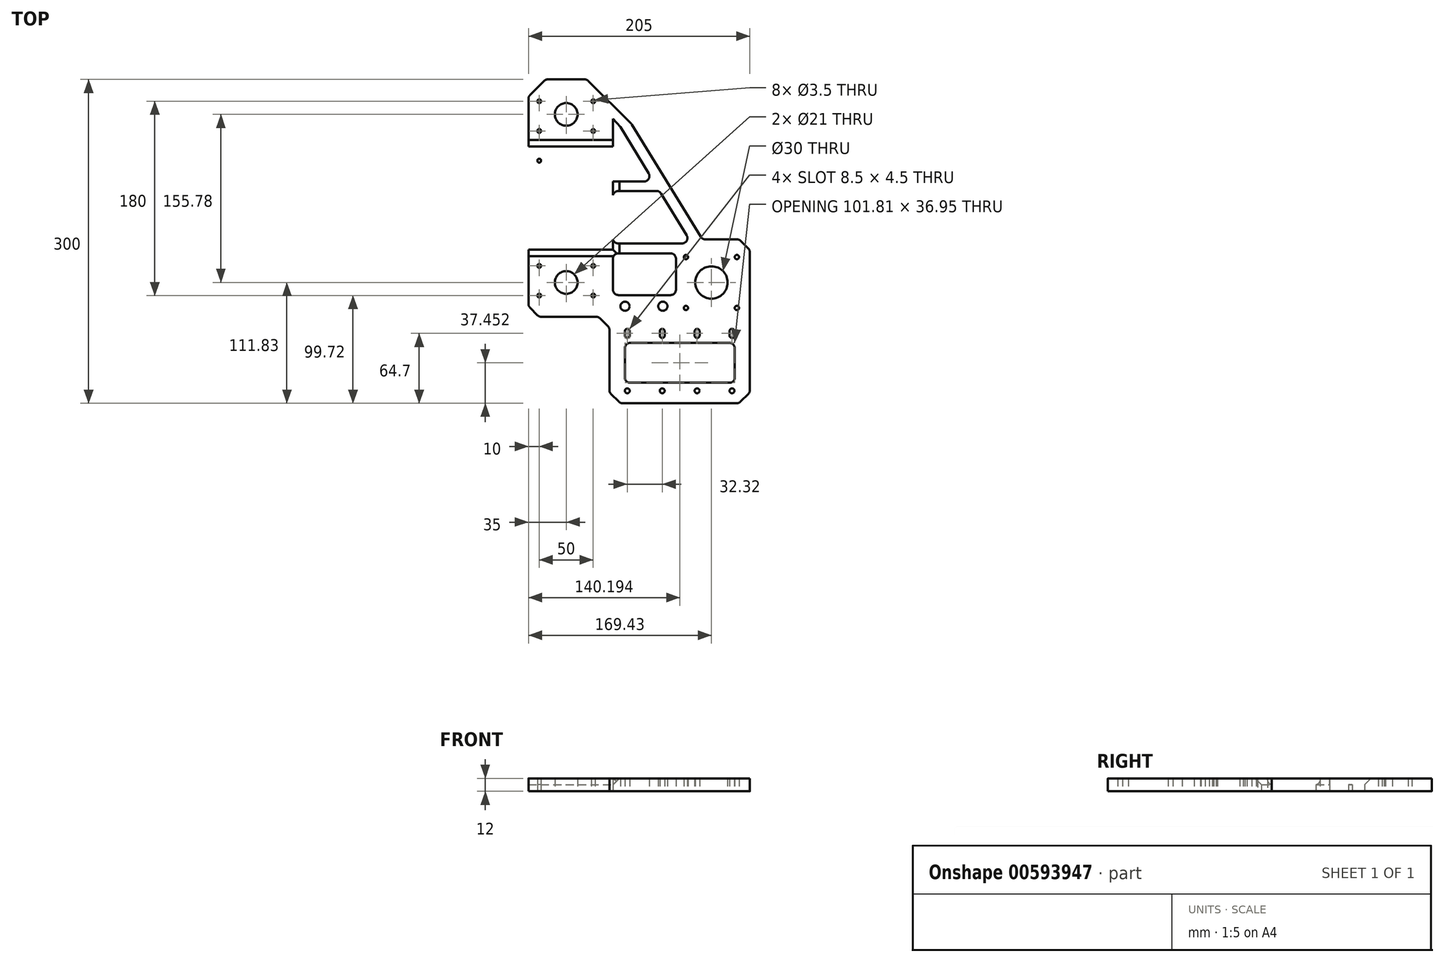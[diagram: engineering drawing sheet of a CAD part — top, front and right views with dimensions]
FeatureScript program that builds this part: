
annotation { "Feature Type Name" : "Feature", "Feature Type Description" : "" }
export const myFeature = defineFeature(function(context is Context, id is Id, definition is map)
    precondition{}
    {
        {
            var Q0;
            Q0=qCreatedBy(makeId("Top.planeOp"),FACE);
            var sketch = newSketch(context, id + "F0", { "sketchPlane" : qUnion([Q0])});
            skLineSegment(sketch, "E0", {"start": v(93.96, -148.54) * mm, "end": v(101.04, -141.46) * mm});
            skLineSegment(sketch, "E1", {"start": v(90.43, -150) * mm, "end": v(-15.43, -150) * mm});
            skLineSegment(sketch, "E2", {"start": v(-26.04, -141.46) * mm, "end": v(-18.96, -148.54) * mm});
            skLineSegment(sketch, "E3", {"start": v(-27.5, -137.93) * mm, "end": v(-27.5, -82.07) * mm});
            skLineSegment(sketch, "E4", {"start": v(-36.04, -71.46) * mm, "end": v(-28.96, -78.54) * mm});
            skLineSegment(sketch, "E5", {"start": v(-39.57, -70) * mm, "end": v(-90.43, -70) * mm});
            skLineSegment(sketch, "E6", {"start": v(-101.04, -61.46) * mm, "end": v(-93.96, -68.54) * mm});
            skLineSegment(sketch, "E7", {"start": v(-102.5, -57.93) * mm, "end": v(-102.5, 131.93) * mm});
            skLineSegment(sketch, "E8", {"start": v(-87.96, 148.54) * mm, "end": v(-101.04, 135.46) * mm});
            skLineSegment(sketch, "E9", {"start": v(-84.43, 150) * mm, "end": v(-50.57, 150) * mm});
            skLineSegment(sketch, "E10", {"start": v(-7.5, 109) * mm, "end": v(-47.04, 148.54) * mm});
            skLineSegment(sketch, "E11", {"start": v(-6.78, 108.09) * mm, "end": v(56.96, 4.21) * mm});
            skLineSegment(sketch, "E12", {"start": v(90.43, 1.83) * mm, "end": v(61.22, 1.83) * mm});
            skLineSegment(sketch, "E13", {"start": v(101.04, -6.7) * mm, "end": v(93.96, 0.37) * mm});
            skLineSegment(sketch, "E14", {"start": v(102.5, -10.24) * mm, "end": v(102.5, -137.93) * mm});
            skLineSegment(sketch, "E15", {"start": v(-13.2, -83.3) * mm, "end": v(-13.2, -87.3) * mm});
            skLineSegment(sketch, "E16", {"start": v(-8.7, -87.3) * mm, "end": v(-8.7, -83.3) * mm});
            skLineSegment(sketch, "E17", {"start": v(19.11, -83.3) * mm, "end": v(19.11, -87.3) * mm});
            skLineSegment(sketch, "E18", {"start": v(23.61, -87.3) * mm, "end": v(23.61, -83.3) * mm});
            skLineSegment(sketch, "E19", {"start": v(51.43, -83.3) * mm, "end": v(51.43, -87.3) * mm});
            skLineSegment(sketch, "E20", {"start": v(55.93, -87.3) * mm, "end": v(55.93, -83.3) * mm});
            skLineSegment(sketch, "E21", {"start": v(83.75, -83.3) * mm, "end": v(83.75, -87.3) * mm});
            skLineSegment(sketch, "E22", {"start": v(88.25, -87.3) * mm, "end": v(88.25, -83.3) * mm});
            skCircle(sketch, "E23", {"center": v(-42.5, 129.72) * mm, "radius": 1.75 * mm});
            skCircle(sketch, "E24", {"center": v(-92.5, 129.72) * mm, "radius": 1.75 * mm});
            skCircle(sketch, "E25", {"center": v(-92.5, 74.72) * mm, "radius": 1.75 * mm});
            skCircle(sketch, "E26", {"center": v(-92.5, 4.72) * mm, "radius": 1.75 * mm});
            skCircle(sketch, "E27", {"center": v(-92.5, -50.28) * mm, "radius": 1.75 * mm});
            skCircle(sketch, "E28", {"center": v(-42.5, -50.28) * mm, "radius": 1.75 * mm});
            skCircle(sketch, "E29", {"center": v(-42.5, 4.72) * mm, "radius": 1.75 * mm});
            skCircle(sketch, "E30", {"center": v(-42.5, 74.72) * mm, "radius": 1.75 * mm});
            skCircle(sketch, "E31", {"center": v(-92.5, 102.22) * mm, "radius": 1.75 * mm});
            skCircle(sketch, "E32", {"center": v(-42.5, 102.22) * mm, "radius": 1.75 * mm});
            skCircle(sketch, "E33", {"center": v(-67.5, 74.72) * mm, "radius": 1.75 * mm});
            skCircle(sketch, "E34", {"center": v(-92.5, 39.72) * mm, "radius": 1.75 * mm});
            skCircle(sketch, "E35", {"center": v(-42.5, 39.72) * mm, "radius": 1.75 * mm});
            skCircle(sketch, "E36", {"center": v(-92.5, -22.78) * mm, "radius": 1.75 * mm});
            skCircle(sketch, "E37", {"center": v(-42.5, -22.78) * mm, "radius": 1.75 * mm});
            skCircle(sketch, "E38", {"center": v(-67.5, 4.72) * mm, "radius": 1.75 * mm});
            skCircle(sketch, "E39", {"center": v(-10.96, -138.5) * mm, "radius": 2.25 * mm});
            skCircle(sketch, "E40", {"center": v(21.36, -138.5) * mm, "radius": 2.25 * mm});
            skCircle(sketch, "E41", {"center": v(53.68, -138.5) * mm, "radius": 2.25 * mm});
            skCircle(sketch, "E42", {"center": v(86, -138.5) * mm, "radius": 2.25 * mm});
            skCircle(sketch, "E43", {"center": v(-67.5, 39.72) * mm, "radius": 15 * mm});
            skCircle(sketch, "E44", {"center": v(-91.07, 63.3) * mm, "radius": 2 * mm});
            skCircle(sketch, "E45", {"center": v(-43.93, 63.3) * mm, "radius": 2 * mm});
            skCircle(sketch, "E46", {"center": v(-43.93, 16.15) * mm, "radius": 2 * mm});
            skCircle(sketch, "E47", {"center": v(-91.07, 16.15) * mm, "radius": 2 * mm});
            skCircle(sketch, "E48", {"center": v(-67.5, -38.17) * mm, "radius": 10.5 * mm});
            skCircle(sketch, "E49", {"center": v(-67.5, 117.61) * mm, "radius": 10.5 * mm});
            skCircle(sketch, "E50", {"center": v(-13.07, -60.17) * mm, "radius": 4.25 * mm});
            skCircle(sketch, "E51", {"center": v(21.93, -60.17) * mm, "radius": 4.25 * mm});
            skCircle(sketch, "E52", {"center": v(43.36, -14.6) * mm, "radius": 2 * mm});
            skCircle(sketch, "E53", {"center": v(90.5, -14.6) * mm, "radius": 2 * mm});
            skCircle(sketch, "E54", {"center": v(90.5, -61.74) * mm, "radius": 2 * mm});
            skCircle(sketch, "E55", {"center": v(43.36, -61.74) * mm, "radius": 2 * mm});
            skCircle(sketch, "E56", {"center": v(66.93, -38.17) * mm, "radius": 15 * mm});
            skArc(sketch, "E57", {"start": v(-8.7, -83.3) * mm, "mid": v(-10.96, -81.05) * mm, "end": v(-13.2, -83.3) * mm});
            skArc(sketch, "E58", {"start": v(-13.2, -87.3) * mm, "mid": v(-10.96, -89.55) * mm, "end": v(-8.7, -87.3) * mm});
            skArc(sketch, "E59", {"start": v(23.61, -83.3) * mm, "mid": v(21.36, -81.05) * mm, "end": v(19.11, -83.3) * mm});
            skArc(sketch, "E60", {"start": v(19.11, -87.3) * mm, "mid": v(21.36, -89.55) * mm, "end": v(23.61, -87.3) * mm});
            skArc(sketch, "E61", {"start": v(55.93, -83.3) * mm, "mid": v(53.68, -81.05) * mm, "end": v(51.43, -83.3) * mm});
            skArc(sketch, "E62", {"start": v(51.43, -87.3) * mm, "mid": v(53.68, -89.55) * mm, "end": v(55.93, -87.3) * mm});
            skArc(sketch, "E63", {"start": v(88.25, -83.3) * mm, "mid": v(86, -81.05) * mm, "end": v(83.75, -83.3) * mm});
            skArc(sketch, "E64", {"start": v(83.75, -87.3) * mm, "mid": v(86, -89.55) * mm, "end": v(88.25, -87.3) * mm});
            skPoint(sketch, "E65.visualSharp", {"position": v(-48.5, 150) * mm});
            skArc(sketch, "E65.filletArc", {"start": v(-47.04, 148.54) * mm, "mid": v(-48.66, 149.62) * mm, "end": v(-50.57, 150) * mm});
            skPoint(sketch, "E66.visualSharp", {"position": v(-86.5, 150) * mm});
            skArc(sketch, "E66.filletArc", {"start": v(-84.43, 150) * mm, "mid": v(-86.34, 149.62) * mm, "end": v(-87.96, 148.54) * mm});
            skPoint(sketch, "E67.visualSharp", {"position": v(-102.5, 134) * mm});
            skArc(sketch, "E67.filletArc", {"start": v(-101.04, 135.46) * mm, "mid": v(-102.12, 133.84) * mm, "end": v(-102.5, 131.93) * mm});
            skPoint(sketch, "E68.visualSharp", {"position": v(-102.5, -60) * mm});
            skArc(sketch, "E68.filletArc", {"start": v(-102.5, -57.93) * mm, "mid": v(-102.12, -59.84) * mm, "end": v(-101.04, -61.46) * mm});
            skPoint(sketch, "E69.visualSharp", {"position": v(-92.5, -70) * mm});
            skArc(sketch, "E69.filletArc", {"start": v(-93.96, -68.54) * mm, "mid": v(-92.34, -69.62) * mm, "end": v(-90.43, -70) * mm});
            skPoint(sketch, "E70.visualSharp", {"position": v(-37.5, -70) * mm});
            skArc(sketch, "E70.filletArc", {"start": v(-36.04, -71.46) * mm, "mid": v(-37.66, -70.38) * mm, "end": v(-39.57, -70) * mm});
            skPoint(sketch, "E71.visualSharp", {"position": v(-27.5, -80) * mm});
            skArc(sketch, "E71.filletArc", {"start": v(-27.5, -82.07) * mm, "mid": v(-27.88, -80.16) * mm, "end": v(-28.96, -78.54) * mm});
            skPoint(sketch, "E72.visualSharp", {"position": v(-27.5, -140) * mm});
            skArc(sketch, "E72.filletArc", {"start": v(-27.5, -137.93) * mm, "mid": v(-27.12, -139.84) * mm, "end": v(-26.04, -141.46) * mm});
            skPoint(sketch, "E73.visualSharp", {"position": v(-17.5, -150) * mm});
            skArc(sketch, "E73.filletArc", {"start": v(-18.96, -148.54) * mm, "mid": v(-17.34, -149.62) * mm, "end": v(-15.43, -150) * mm});
            skPoint(sketch, "E74.visualSharp", {"position": v(92.5, -150) * mm});
            skArc(sketch, "E74.filletArc", {"start": v(90.43, -150) * mm, "mid": v(92.34, -149.62) * mm, "end": v(93.96, -148.54) * mm});
            skPoint(sketch, "E75.visualSharp", {"position": v(102.5, -140) * mm});
            skArc(sketch, "E75.filletArc", {"start": v(101.04, -141.46) * mm, "mid": v(102.12, -139.84) * mm, "end": v(102.5, -137.93) * mm});
            skPoint(sketch, "E76.visualSharp", {"position": v(102.5, -8.17) * mm});
            skArc(sketch, "E76.filletArc", {"start": v(102.5, -10.24) * mm, "mid": v(102.12, -8.33) * mm, "end": v(101.04, -6.7) * mm});
            skPoint(sketch, "E77.visualSharp", {"position": v(92.5, 1.83) * mm});
            skArc(sketch, "E77.filletArc", {"start": v(93.96, 0.37) * mm, "mid": v(92.34, 1.45) * mm, "end": v(90.43, 1.83) * mm});
            skPoint(sketch, "E78.visualSharp", {"position": v(58.42, 1.83) * mm});
            skArc(sketch, "E78.filletArc", {"start": v(56.96, 4.21) * mm, "mid": v(58.78, 2.47) * mm, "end": v(61.22, 1.83) * mm});
            skPoint(sketch, "E79.visualSharp", {"position": v(-7.09, 108.59) * mm});
            skArc(sketch, "E79.filletArc", {"start": v(-6.78, 108.09) * mm, "mid": v(-7.12, 108.57) * mm, "end": v(-7.5, 109) * mm});
            skLineSegment(sketch, "E80.0", {"start": v(-97.5, -57.93) * mm, "end": v(-90.43, -65) * mm});
            skLineSegment(sketch, "E81.0", {"start": v(-22.5, -137.93) * mm, "end": v(-15.43, -145) * mm});
            skLineSegment(sketch, "E82.0", {"start": v(-32.5, -67.93) * mm, "end": v(-25.43, -75) * mm});
            skLineSegment(sketch, "E83.0", {"start": v(90.43, -145) * mm, "end": v(97.5, -137.93) * mm});
            skArc(sketch, "E84.0", {"start": v(-22.5, -82.07) * mm, "mid": v(-23.26, -78.24) * mm, "end": v(-25.43, -75) * mm});
            skArc(sketch, "E85.0", {"start": v(-32.5, -67.93) * mm, "mid": v(-35.74, -65.76) * mm, "end": v(-39.57, -65) * mm});
            skLineSegment(sketch, "E86", {"start": v(-24.24, -16.15) * mm, "end": v(-24.24, -44.82) * mm});
            skLineSegment(sketch, "E87", {"start": v(-19.24, -49.82) * mm, "end": v(29.08, -49.82) * mm});
            skLineSegment(sketch, "E88", {"start": v(34.08, -44.82) * mm, "end": v(34.08, -16.15) * mm});
            skLineSegment(sketch, "E89", {"start": v(-19.24, -11.15) * mm, "end": v(29.08, -11.15) * mm});
            skLineSegment(sketch, "E90.bottom", {"start": v(-8.2, -94.07) * mm, "end": v(83.6, -94.07) * mm});
            skLineSegment(sketch, "E90.top", {"start": v(-8.2, -131.02) * mm, "end": v(83.6, -131.02) * mm});
            skLineSegment(sketch, "E90.left", {"start": v(-13.2, -99.07) * mm, "end": v(-13.2, -126.02) * mm});
            skLineSegment(sketch, "E90.right", {"start": v(88.6, -99.07) * mm, "end": v(88.6, -126.02) * mm});
            skPoint(sketch, "E91.visualSharp", {"position": v(-13.2, -94.07) * mm});
            skArc(sketch, "E91.filletArc", {"start": v(-8.2, -94.07) * mm, "mid": v(-11.75, -95.54) * mm, "end": v(-13.2, -99.07) * mm});
            skPoint(sketch, "E92.visualSharp", {"position": v(-13.2, -131.02) * mm});
            skArc(sketch, "E92.filletArc", {"start": v(-13.2, -126.02) * mm, "mid": v(-11.75, -129.56) * mm, "end": v(-8.2, -131.02) * mm});
            skPoint(sketch, "E93.visualSharp", {"position": v(88.6, -94.07) * mm});
            skArc(sketch, "E93.filletArc", {"start": v(88.6, -99.07) * mm, "mid": v(87.13, -95.54) * mm, "end": v(83.6, -94.07) * mm});
            skPoint(sketch, "E94.visualSharp", {"position": v(88.6, -131.02) * mm});
            skArc(sketch, "E94.filletArc", {"start": v(83.6, -131.02) * mm, "mid": v(87.13, -129.56) * mm, "end": v(88.6, -126.02) * mm});
            skPoint(sketch, "E95.visualSharp", {"position": v(34.08, -49.82) * mm});
            skArc(sketch, "E95.filletArc", {"start": v(29.08, -49.82) * mm, "mid": v(32.61, -48.36) * mm, "end": v(34.08, -44.82) * mm});
            skPoint(sketch, "E96.visualSharp", {"position": v(34.08, -11.15) * mm});
            skArc(sketch, "E96.filletArc", {"start": v(34.08, -16.15) * mm, "mid": v(32.61, -12.62) * mm, "end": v(29.08, -11.15) * mm});
            skPoint(sketch, "E97.visualSharp", {"position": v(-24.24, -11.15) * mm});
            skArc(sketch, "E97.filletArc", {"start": v(-19.24, -11.15) * mm, "mid": v(-22.78, -12.62) * mm, "end": v(-24.24, -16.15) * mm});
            skPoint(sketch, "E98.visualSharp", {"position": v(-24.24, -49.82) * mm});
            skArc(sketch, "E98.filletArc", {"start": v(-24.24, -44.82) * mm, "mid": v(-22.78, -48.36) * mm, "end": v(-19.24, -49.82) * mm});
            skPoint(sketch, "E99.startSnap0", {"position": v(-27.27, 128.77) * mm});
            skLineSegment(sketch, "E100", {"start": v(8.82, 63.03) * mm, "end": v(-17.32, 105.78) * mm});
            skLineSegment(sketch, "E101", {"start": v(-21.43, 108.17) * mm, "end": v(-21.83, 108.18) * mm});
            skLineSegment(sketch, "E102", {"start": v(-24.38, 41.55) * mm, "end": v(-24.38, 3.04) * mm});
            skLineSegment(sketch, "E103", {"start": v(-19.38, -1.96) * mm, "end": v(39.7, -1.96) * mm});
            skLineSegment(sketch, "E104", {"start": v(43.96, 5.66) * mm, "end": v(20.28, 44.26) * mm});
            skLineSegment(sketch, "E105", {"start": v(16, 46.65) * mm, "end": v(-19.4, 46.55) * mm});
            skPoint(sketch, "E106.visualSharp", {"position": v(13.47, 55.42) * mm});
            skArc(sketch, "E106.filletArc", {"start": v(4.55, 55.42) * mm, "mid": v(8.92, 57.97) * mm, "end": v(8.82, 63.03) * mm});
            skPoint(sketch, "E107.visualSharp", {"position": v(18.8, 46.65) * mm});
            skArc(sketch, "E107.filletArc", {"start": v(20.28, 44.26) * mm, "mid": v(18.45, 46.01) * mm, "end": v(16, 46.65) * mm});
            skPoint(sketch, "E108.visualSharp", {"position": v(-24.38, 46.53) * mm});
            skArc(sketch, "E108.filletArc", {"start": v(-19.4, 46.55) * mm, "mid": v(-22.92, 45.08) * mm, "end": v(-24.38, 41.55) * mm});
            skPoint(sketch, "E109.visualSharp", {"position": v(-24.38, -1.96) * mm});
            skArc(sketch, "E109.filletArc", {"start": v(-24.38, 3.04) * mm, "mid": v(-22.92, -0.5) * mm, "end": v(-19.38, -1.96) * mm});
            skPoint(sketch, "E110.visualSharp", {"position": v(48.64, -1.96) * mm});
            skArc(sketch, "E110.filletArc", {"start": v(39.7, -1.96) * mm, "mid": v(44.06, 0.6) * mm, "end": v(43.96, 5.66) * mm});
            skPoint(sketch, "E111.oppositeSnap0", {"position": v(-24.24, -30.49) * mm});
            skLineSegment(sketch, "E111.bottom", {"start": v(-102.5, 87.73) * mm, "end": v(-24.24, 87.73) * mm});
            skLineSegment(sketch, "E111.top", {"start": v(-102.5, -7.77) * mm, "end": v(-24.24, -7.77) * mm});
            skLineSegment(sketch, "E111.left", {"start": v(-102.5, 87.73) * mm, "end": v(-102.5, -7.77) * mm});
            skLineSegment(sketch, "E111.right", {"start": v(-24.24, 87.73) * mm, "end": v(-24.24, -7.77) * mm});
            skLineSegment(sketch, "E112", {"start": v(4.55, 55.42) * mm, "end": v(-24.24, 55.42) * mm});
            skLineSegment(sketch, "E113", {"start": v(-24.24, 55.42) * mm, "end": v(-24.24, 113.42) * mm});
            skLineSegment(sketch, "E114", {"start": v(-24.24, 113.42) * mm, "end": v(-17.32, 105.78) * mm});
            skSolve(sketch);
        }
        {
            var Q0;
            Q0=makeQuery(id+"F0.imprint","IMPRINT",FACE,{"disambiguationData":[TD([[makeQuery(id+"F0.imprint","IMPRINT",EDGE,{"derivedFrom":sQuery(id+"F0.wireOp",EDGE,"E0")}),1.0]])]});
            extrude(context, id + "F1", {"entities" : qUnion([Q0]), "depth" : 12 * mm, "offsetDistance" : 25 * mm});
        }
        {
            var Q0;
            Q0=makeQuery(id+"F0.imprint","IMPRINT",FACE,{"disambiguationData":[TD([[makeQuery(id+"F0.imprint","IMPRINT",EDGE,{"derivedFrom":sQuery(id+"F0.wireOp",EDGE,"E25")}),1.0]])]});
            extrude(context, id + "F2", {"entities" : qUnion([Q0]), "operationType" : NewBodyOperationType.ADD, "depth" : 6 * mm, "offsetDistance" : 25 * mm});
        }
        {
            var Q0;
            {var subQ0=sQuery(id+"F0.wireOp",EDGE,"E111.right");Q0=makeQuery(id+"F1.opExtrude","CAP_EDGE",EDGE,{"disambiguationData":[OSD([subQ0]),TDD([makeQuery(id+"F0.imprint","IMPRINT",EDGE,{"disambiguationData":[TD([[makeQuery(id+"F0.imprint","INTERSECT",VERTEX,{"derivedFrom":[sQuery(id+"F0.wireOp",EDGE,"E108.filletArc"),subQ0]}),1.0]])],"derivedFrom":subQ0})])],"isStart":false});}
            var Q1;
            {var subQ0=sQuery(id+"F0.wireOp",EDGE,"E111.right");Q1=makeQuery(id+"F1.opExtrude","CAP_EDGE",EDGE,{"disambiguationData":[OSD([subQ0]),TDD([makeQuery(id+"F0.imprint","IMPRINT",EDGE,{"disambiguationData":[TD([[makeQuery(id+"F0.imprint","INTERSECT",VERTEX,{"derivedFrom":[sQuery(id+"F0.wireOp",EDGE,"E111.top"),subQ0]}),1.0]])],"derivedFrom":subQ0})])],"isStart":false});}
            var Q2;
            Q2=makeQuery(id+"F1.opExtrude","CAP_EDGE",EDGE,{"disambiguationData":[OSD([sQuery(id+"F0.wireOp",EDGE,"E111.bottom")])],"isStart":false});
            var Q3;
            Q3=makeQuery(id+"F1.opExtrude","CAP_EDGE",EDGE,{"disambiguationData":[OSD([sQuery(id+"F0.wireOp",EDGE,"E111.top")])],"isStart":false});
            chamfer(context, id + "F3", {"entities" : qUnion([Q0, Q1, Q2, Q3]), "width" : 6 * mm, "tangentPropagation" : true});
        }
    });
